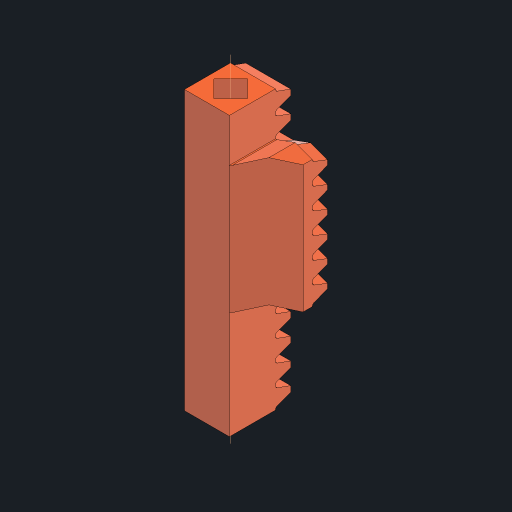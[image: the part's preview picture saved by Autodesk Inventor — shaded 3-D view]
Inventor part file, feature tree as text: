
AUTODESK INVENTOR PART (.ipt)
format: ipt  version: 2023.2 (Build 272271030, 271C)  size: 680,960 bytes
history: native  units: mm
features: sketch x6, projected_geometry x5, extrude x4, sweep x1, pattern_linear x1, other x1, chamfer x1
ambient origin geometry x8: Origin, YZ Plane, XZ Plane, XY Plane, X Axis, Y Axis, Z Axis, Center Point
bodies: Solid1 (feature_tree)
feature tree (19):
  extrude  "Extrusion1"  Depth=40.840704mm
  sweep  "Sweep1"
  pattern_linear  "Rectangular Pattern1"  Spacing1=7.0mm  [1 undecoded]
  sketch  "Sketch4"  dims[d6=1.570796mm]
  extrude  "Extrusion7"  Depth=5.4mm
  extrude  "Extrusion8"  Depth=5.4mm
  extrude  "Extrusion9"  TaperAngle=0.0deg  [1 undecoded]
  other  "Work Axis1"
  chamfer  "Chamfer2"  Distance=140.0mm
  sketch  "Sketch1"  dims[d0=12.0mm d1=40.840704mm]
  sketch  "Sketch2"  dims[d2=9.0mm d3=0.0mm d4=1.0mm]
  projected_geometry  "Projected Loop1"
  sketch  "Sketch3"  dims[d5=1.25mm]
  projected_geometry  "Projected Loop2"
  sketch  "Sketch8"  dims[d7=12.217305mm]
  projected_geometry  "Projected Loop21"
  sketch  "Sketch9"  dims[d17=0.38mm d27=7.0mm d28=5.0mm d29=3.490659mm d30=0.0mm d31=0.0mm d32=140.0mm d34=3.141593mm d49=10.0mm d50=0.0mm d56=0.0mm d57=0.0mm d58=0.0mm d59=0.0mm d60=3.5mm d61=3.3mm d62=5.5mm d63=6.6mm d64=5.4mm d65=2.0mm d66=45.0deg d43=0.5mm d44=0.872665mm d45=0.5mm d46=0.872665mm]
  projected_geometry  "Projected Loop22"
  projected_geometry  "Projected Loop23"
note: 2 required parameter values undecoded (feature->parameter linkage not recoverable at this tier; creation-order binding heuristic only, values carry confidence <= 0.55)
